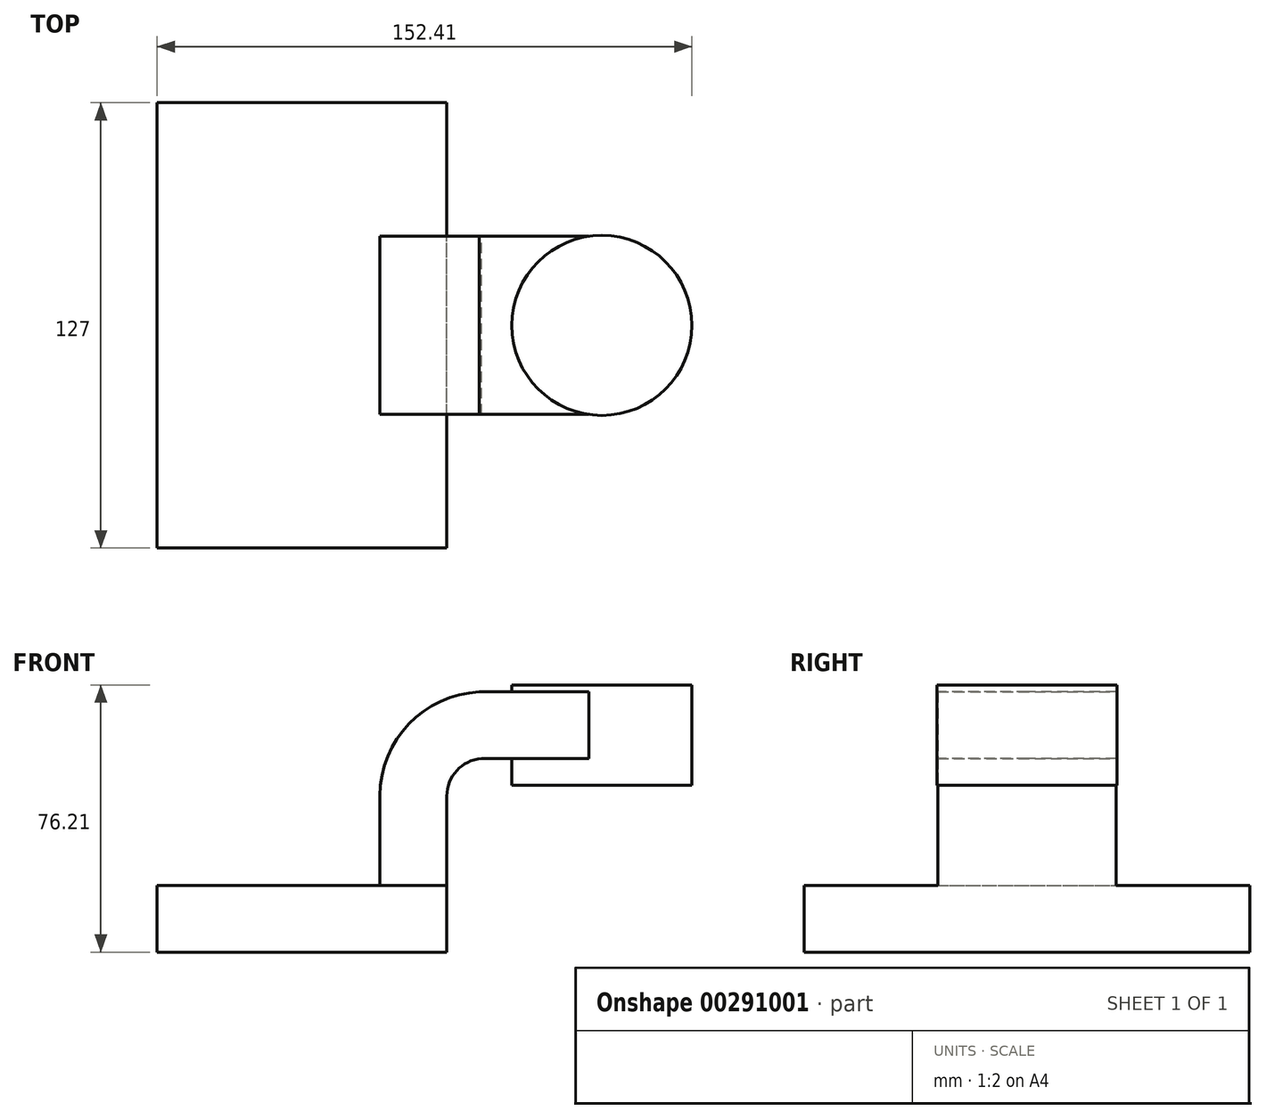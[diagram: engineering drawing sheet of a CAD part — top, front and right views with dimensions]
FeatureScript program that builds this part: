
annotation { "Feature Type Name" : "Feature", "Feature Type Description" : "" }
export const myFeature = defineFeature(function(context is Context, id is Id, definition is map)
    precondition{}
    {
        {
            var Q0;
            Q0=qCreatedBy(makeId("Front.planeOp"),FACE);
            var sketch = newSketch(context, id + "F0", { "sketchPlane" : qUnion([Q0])});
            skLineSegment(sketch, "E0.bottom", {"start": v(-41.28, -9.53) * mm, "end": v(41.28, -9.53) * mm});
            skLineSegment(sketch, "E0.top", {"start": v(-41.28, 9.53) * mm, "end": v(41.28, 9.53) * mm});
            skLineSegment(sketch, "E0.left", {"start": v(-41.28, -9.53) * mm, "end": v(-41.28, 9.53) * mm});
            skLineSegment(sketch, "E0.right", {"start": v(41.28, -9.53) * mm, "end": v(41.28, 9.53) * mm});
            skPoint(sketch, "E0.middle", {"position": v(0, 0) * mm});
            skLineSegment(sketch, "E1.bottom", {"start": v(60.32, 38.1) * mm, "end": v(111.12, 38.1) * mm});
            skLineSegment(sketch, "E1.top", {"start": v(60.32, 66.68) * mm, "end": v(111.12, 66.68) * mm});
            skLineSegment(sketch, "E1.left", {"start": v(60.32, 38.1) * mm, "end": v(60.32, 66.67) * mm});
            skLineSegment(sketch, "E1.right", {"start": v(111.12, 38.1) * mm, "end": v(111.12, 66.67) * mm});
            skPoint(sketch, "E1.middle", {"position": v(85.72, 52.39) * mm});
            skLineSegment(sketch, "E2", {"start": v(41.27, 9.53) * mm, "end": v(41.27, 35.04) * mm});
            skArc(sketch, "E3", {"start": v(41.27, 35.04) * mm, "mid": v(44.11, 42.26) * mm, "end": v(51.1, 45.61) * mm});
            skLineSegment(sketch, "E4", {"start": v(51.1, 45.61) * mm, "end": v(85.46, 45.61) * mm});
            skLineSegment(sketch, "E5.0", {"start": v(50.58, 64.66) * mm, "end": v(85.46, 64.66) * mm});
            skArc(sketch, "E5.1", {"start": v(22.23, 35.04) * mm, "mid": v(30.46, 55.55) * mm, "end": v(50.58, 64.66) * mm});
            skLineSegment(sketch, "E5.2", {"start": v(22.22, 9.53) * mm, "end": v(22.22, 35.04) * mm});
            skLineSegment(sketch, "E6", {"start": v(85.46, 64.66) * mm, "end": v(85.46, 66.68) * mm});
            skLineSegment(sketch, "E7", {"start": v(85.46, 45.61) * mm, "end": v(85.46, 38.1) * mm});
            skLineSegment(sketch, "E8", {"start": v(85.46, 38.1) * mm, "end": v(85.46, 66.68) * mm});
            skFitSpline(sketch, "E9", {"points": [v(-41.28, 9.53) * mm, v(50.58, 64.66) * mm], "startDerivative": vector(1.82, 47.55) * mm, "endDerivative": vector(70.4, 1.19) * mm});
            skSolve(sketch);
        }
        {
            var Q0;
            Q0=makeQuery(id+"F0.imprint","IMPRINT",FACE,{"disambiguationData":[TD([[makeQuery(id+"F0.imprint","IMPRINT",EDGE,{"derivedFrom":sQuery(id+"F0.wireOp",EDGE,"E0.bottom")}),1.0]])]});
            extrude(context, id + "F1", {"entities" : qUnion([Q0]), "endBound" : BoundingType.SYMMETRIC, "depth" : 127 * mm});
        }
        {
            var Q0;
            {var subQ1=sQuery(id+"F0.wireOp",EDGE,"E2");Q0=makeQuery(id+"F0.imprint","IMPRINT",FACE,{"disambiguationData":[TD([[makeQuery(id+"F0.imprint","IMPRINT",EDGE,{"derivedFrom":subQ1}),1.0]])]});}
            var Q1;
            {var subQ0=sQuery(id+"F0.wireOp",EDGE,"E4");var subQ1=sQuery(id+"F0.wireOp",EDGE,"E1.left");var subQ2=makeQuery(id+"F0.imprint","INTERSECT",VERTEX,{"derivedFrom":[subQ1,subQ0]});Q1=makeQuery(id+"F0.imprint","IMPRINT",FACE,{"disambiguationData":[TD([[makeQuery(id+"F0.imprint","IMPRINT",EDGE,{"disambiguationData":[TD([[subQ2,-1.0]])],"derivedFrom":subQ1}),-1.0]])]});}
            extrude(context, id + "F2", {"entities" : qUnion([Q0, Q1]), "operationType" : NewBodyOperationType.ADD, "endBound" : BoundingType.SYMMETRIC, "depth" : 50.8 * mm});
        }
        {
            var Q0;
            Q0=makeQuery(id+"F0.imprint","IMPRINT",FACE,{"disambiguationData":[TD([[makeQuery(id+"F0.imprint","IMPRINT",EDGE,{"derivedFrom":sQuery(id+"F0.wireOp",EDGE,"E5.1")}),1.0]])]});
            extrude(context, id + "F3", {"entities" : qUnion([Q0]), "operationType" : NewBodyOperationType.ADD, "endBound" : BoundingType.SYMMETRIC, "depth" : 15.88 * mm});
        }
        {
            var Q0;
            {var subQ0=sQuery(id+"F0.wireOp",EDGE,"E1.right");Q0=makeQuery(id+"F0.imprint","IMPRINT",FACE,{"disambiguationData":[TD([[makeQuery(id+"F0.imprint","IMPRINT",EDGE,{"derivedFrom":subQ0}),1.0]])]});}
            var Q1;
            Q1=sQuery(id+"F0.wireOp",EDGE,"E8");
            revolve(context, id + "F4", {"operationType" : NewBodyOperationType.ADD, "entities" : qUnion([Q0]), "axis" : qUnion([Q1]), "revolveType" : RevolveType.FULL});
        }
    });
